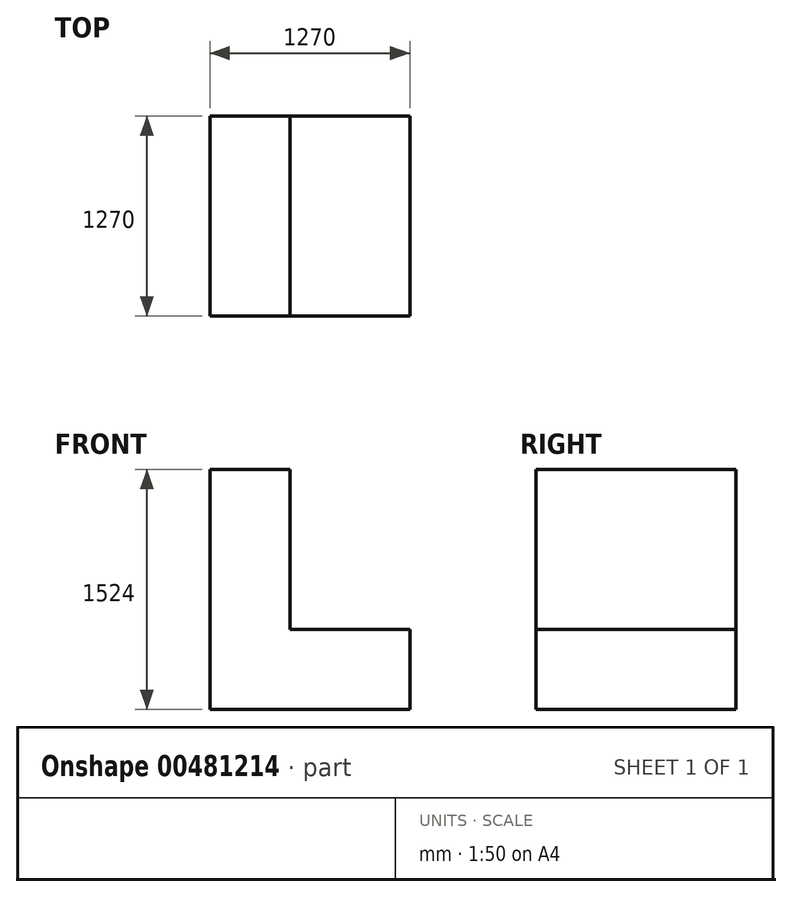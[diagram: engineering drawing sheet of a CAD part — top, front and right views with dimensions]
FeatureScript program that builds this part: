
annotation { "Feature Type Name" : "Feature", "Feature Type Description" : "" }
export const myFeature = defineFeature(function(context is Context, id is Id, definition is map)
    precondition{}
    {
        {
            var Q0;
            Q0=qCreatedBy(makeId("Front.planeOp"),FACE);
            var sketch = newSketch(context, id + "F0", { "sketchPlane" : qUnion([Q0])});
            skLineSegment(sketch, "E0", {"start": v(0, 0) * mm, "end": v(0, 1524) * mm});
            skLineSegment(sketch, "E1", {"start": v(0, 1524) * mm, "end": v(508, 1524) * mm});
            skLineSegment(sketch, "E2", {"start": v(508, 1524) * mm, "end": v(508, 508) * mm});
            skLineSegment(sketch, "E3", {"start": v(508, 508) * mm, "end": v(1270, 508) * mm});
            skLineSegment(sketch, "E4", {"start": v(1270, 508) * mm, "end": v(1270, 0) * mm});
            skLineSegment(sketch, "E5", {"start": v(0, 0) * mm, "end": v(1270, 0) * mm});
            skSolve(sketch);
        }
        {
            var Q0;
            Q0=makeQuery(id+"F0.imprint","IMPRINT",FACE,{"disambiguationData":[TD([[makeQuery(id+"F0.imprint","IMPRINT",EDGE,{"derivedFrom":sQuery(id+"F0.wireOp",EDGE,"E0")}),-1.0]])]});
            extrude(context, id + "F1", {"entities" : qUnion([Q0]), "depth" : 1270 * mm});
        }
    });
